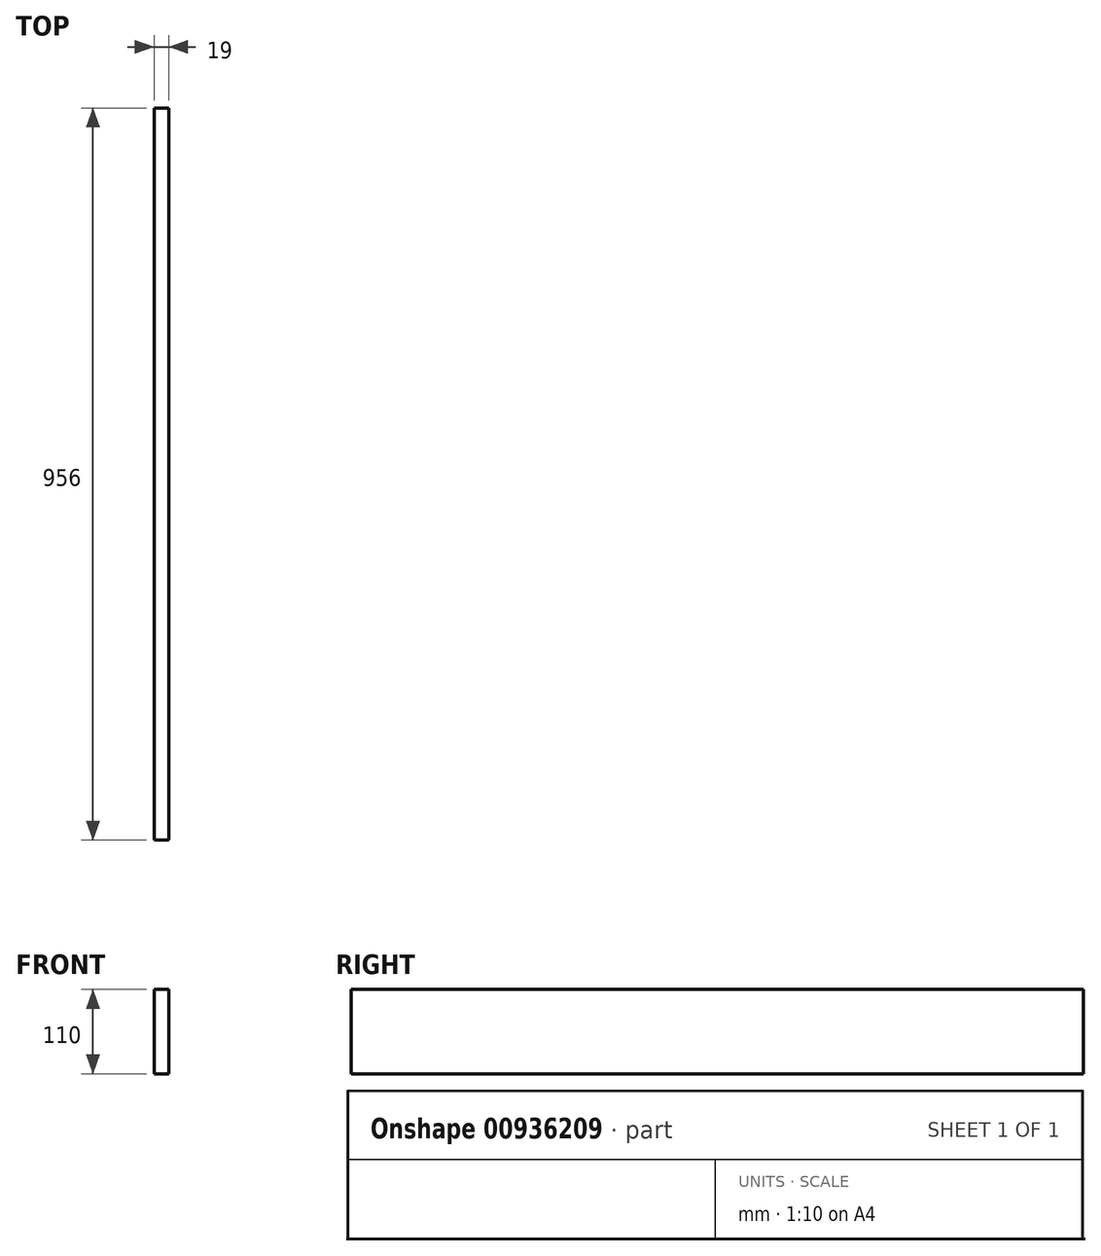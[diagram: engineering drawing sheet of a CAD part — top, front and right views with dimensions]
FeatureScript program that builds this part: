
annotation { "Feature Type Name" : "Feature", "Feature Type Description" : "" }
export const myFeature = defineFeature(function(context is Context, id is Id, definition is map)
    precondition{}
    {
        {
            var Q0;
            Q0=qCreatedBy(makeId("Front.planeOp"),FACE);
            var sketch = newSketch(context, id + "F0", { "sketchPlane" : qUnion([Q0])});
            skLineSegment(sketch, "E0.bottom", {"start": v(0, 0) * mm, "end": v(19, 0) * mm});
            skLineSegment(sketch, "E0.top", {"start": v(0, 110) * mm, "end": v(19, 110) * mm});
            skLineSegment(sketch, "E0.left", {"start": v(0, 0) * mm, "end": v(0, 110) * mm});
            skLineSegment(sketch, "E0.right", {"start": v(19, 0) * mm, "end": v(19, 110) * mm});
            skSolve(sketch);
        }
        {
            var Q0;
            Q0=qSketchRegion(id+"F0",true);
            extrude(context, id + "F1", {"entities" : qUnion([Q0]), "depth" : 956 * mm, "offsetDistance" : 25 * mm});
        }
    });
